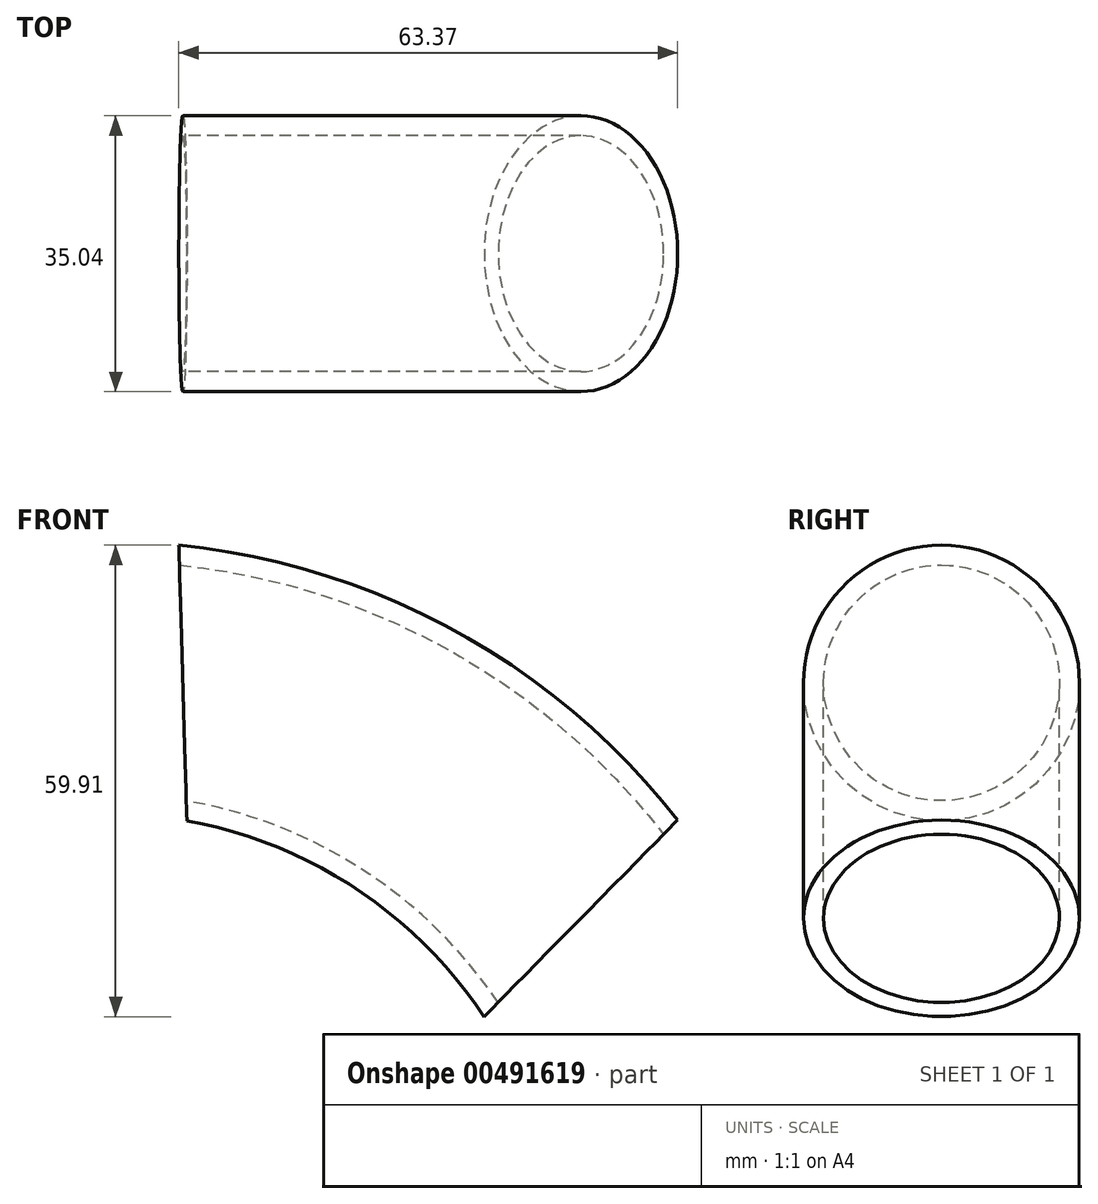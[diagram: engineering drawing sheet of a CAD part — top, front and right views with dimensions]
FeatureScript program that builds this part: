
annotation { "Feature Type Name" : "Feature", "Feature Type Description" : "" }
export const myFeature = defineFeature(function(context is Context, id is Id, definition is map)
    precondition{}
    {
        {
            var Q0;
            Q0=qCreatedBy(makeId("Front.planeOp"),FACE);
            var sketch = newSketch(context, id + "F0", { "sketchPlane" : qUnion([Q0])});
            skPoint(sketch, "E0.visualSharp", {"position": v(-73.66, -32.82) * mm});
            skPoint(sketch, "E1.visualSharp", {"position": v(-33.1, -72.77) * mm});
            skPoint(sketch, "E2.visualSharp", {"position": v(65.04, 26.86) * mm});
            skPoint(sketch, "E3.visualSharp", {"position": v(24.49, 66.81) * mm});
            skArc(sketch, "E4.1", {"start": v(-27.44, -62.56) * mm, "mid": v(-64.18, -61.63) * mm, "end": v(-61.6, -24.97) * mm});
            skArc(sketch, "E4.5", {"start": v(17.78, 55.67) * mm, "mid": v(62.52, 53.43) * mm, "end": v(60.49, 8.68) * mm});
            skLineSegment(sketch, "E5", {"start": v(-61.6, -24.97) * mm, "end": v(17.78, 55.67) * mm});
            skLineSegment(sketch, "E6", {"start": v(-27.44, -62.56) * mm, "end": v(60.49, 8.68) * mm});
            skLineSegment(sketch, "E7.0", {"start": v(-59.54, -27.22) * mm, "end": v(19.88, 53.46) * mm});
            skArc(sketch, "E7.1", {"start": v(-29.48, -60.3) * mm, "mid": v(-61.92, -59.58) * mm, "end": v(-59.54, -27.22) * mm});
            skLineSegment(sketch, "E7.2", {"start": v(-29.48, -60.3) * mm, "end": v(58.5, 10.99) * mm});
            skArc(sketch, "E7.3", {"start": v(19.88, 53.46) * mm, "mid": v(60.26, 51.38) * mm, "end": v(58.5, 10.99) * mm});
            skLineSegment(sketch, "E8", {"start": v(-61.6, -24.97) * mm, "end": v(-21.91, 15.35) * mm});
            skLineSegment(sketch, "E9", {"start": v(-21.91, 15.35) * mm, "end": v(16.53, -26.94) * mm});
            skLineSegment(sketch, "E10", {"start": v(17.78, 55.67) * mm, "end": v(19.88, 53.46) * mm});
            skLineSegment(sketch, "E11", {"start": v(58.5, 10.99) * mm, "end": v(60.49, 8.68) * mm});
            skArc(sketch, "E12", {"start": v(0, 37.61) * mm, "mid": v(-22.2, 57.72) * mm, "end": v(-50.53, 67.5) * mm});
            skLineSegment(sketch, "E13", {"start": v(0, 0) * mm, "end": v(-68.03, 0) * mm});
            skSolve(sketch);
        }
        {
            var Q0;
            Q0=sQuery(id+"F0.wireOp",EDGE,"E5");
            cPlane(context, id + "F1", {"entities" : qUnion([Q0]), "cplaneType" : CPlaneType.LINE_ANGLE, "offset" : 25.4 * mm, "angle" : 90 * degree, "width" : 152.4 * mm, "height" : 152.4 * mm});
        }
        {
            var Q0;
            Q0=qCreatedBy(id+"F1.planeOp",FACE);
            var sketch = newSketch(context, id + "F2", { "sketchPlane" : qUnion([Q0])});
            skLineSegment(sketch, "E14", {"start": v(0, 26.84) * mm, "end": v(0, 48.35) * mm});
            skCircle(sketch, "E15", {"center": v(0, 26.84) * mm, "radius": 17.52 * mm});
            skSolve(sketch);
        }
        {
            var Q0;
            Q0=makeQuery(id+"F2.imprint","IMPRINT",FACE,{"disambiguationData":[TD([[makeQuery(id+"F2.imprint","IMPRINT",EDGE,{"derivedFrom":sQuery(id+"F2.wireOp",EDGE,"E15")}),1.0]])]});
            var Q1;
            Q1=sQuery(id+"F0.wireOp",EDGE,"nKpo33eE-IB5t-xdRZ-u1jk-F7Vzt1Kr22UI");
            var Q2;
            Q2=sQuery(id+"F0.wireOp",EDGE,"E12");
            sweep(context, id + "F3", {"profiles" : qUnion([Q0]), "path" : qUnion([Q1, Q2])});
        }
        {
            var Q0;
            Q0=makeQuery(id+"F3.opSweep","CAP_FACE",FACE,{"disambiguationData":[OSD([sQuery(id+"F0.wireOp",VERTEX,"nKpo33eE-IB5t-xdRZ-u1jk-F7Vzt1Kr22UI.end"),sQuery(id+"F2.wireOp",EDGE,"E15")])],"isStart":false});
            var sketch = newSketch(context, id + "F4", { "sketchPlane" : qUnion([Q0])});
            skCircle(sketch, "E16.0", {"center": v(0, 69) * mm, "radius": 14.98 * mm});
            skSolve(sketch);
        }
        {
            var Q0;
            Q0=makeQuery(id+"F4.imprint","IMPRINT",FACE,{"disambiguationData":[TD([[makeQuery(id+"F4.imprint","IMPRINT",EDGE,{"derivedFrom":sQuery(id+"F4.wireOp",EDGE,"E16.0")}),1.0]])]});
            var Q1;
            Q1=sQuery(id+"F0.wireOp",EDGE,"qCj8Zapl-fwVA-ZPwK-KBk3-chwa6JRhFakC");
            var Q2;
            Q2=sQuery(id+"F0.wireOp",EDGE,"E12");
            sweep(context, id + "F5", {"operationType" : NewBodyOperationType.REMOVE, "profiles" : qUnion([Q0]), "path" : qUnion([Q1, Q2])});
        }
    });
